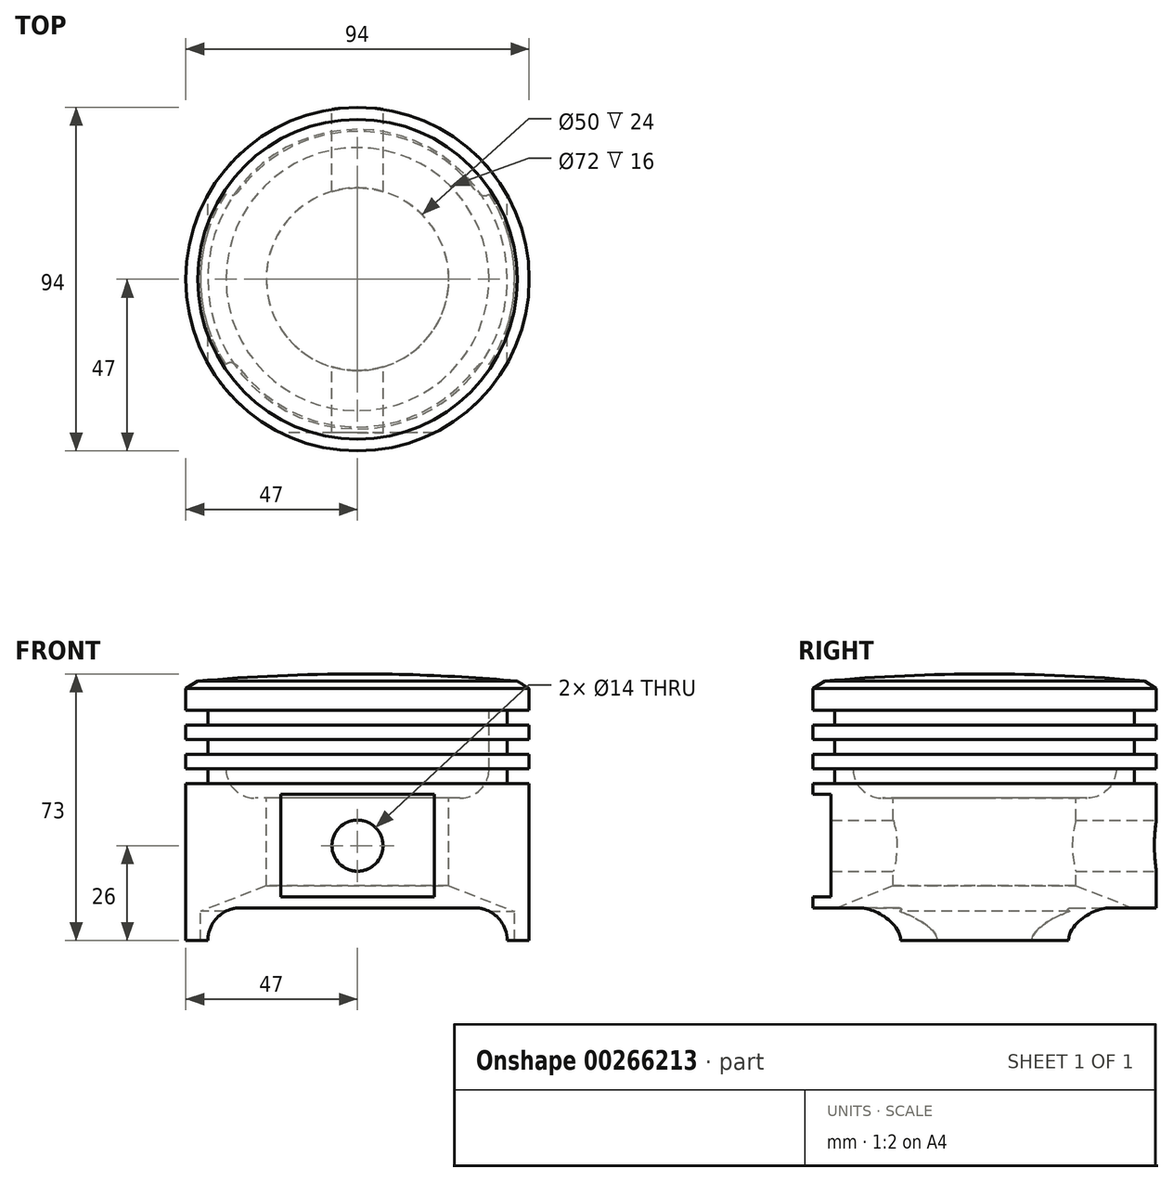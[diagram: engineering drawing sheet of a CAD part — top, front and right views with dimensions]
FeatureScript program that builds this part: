
annotation { "Feature Type Name" : "Feature", "Feature Type Description" : "" }
export const myFeature = defineFeature(function(context is Context, id is Id, definition is map)
    precondition{}
    {
        {
            var Q0;
            Q0=qCreatedBy(makeId("Front.planeOp"),FACE);
            var sketch = newSketch(context, id + "F0", { "sketchPlane" : qUnion([Q0])});
            skLineSegment(sketch, "E0", {"start": v(43.74, 89) * mm, "end": v(47, 87) * mm});
            skLineSegment(sketch, "E1", {"start": v(47, 87) * mm, "end": v(47, 81) * mm});
            skLineSegment(sketch, "E2", {"start": v(47, 81) * mm, "end": v(41, 81) * mm});
            skLineSegment(sketch, "E3", {"start": v(41, 81) * mm, "end": v(41, 77) * mm});
            skLineSegment(sketch, "E4", {"start": v(41, 77) * mm, "end": v(47, 77) * mm});
            skLineSegment(sketch, "E5", {"start": v(47, 77) * mm, "end": v(47, 73) * mm});
            skLineSegment(sketch, "E6", {"start": v(47, 73) * mm, "end": v(41, 73) * mm});
            skLineSegment(sketch, "E7", {"start": v(41, 73) * mm, "end": v(41, 69) * mm});
            skLineSegment(sketch, "E8", {"start": v(41, 69) * mm, "end": v(47, 69) * mm});
            skLineSegment(sketch, "E9", {"start": v(47, 69) * mm, "end": v(47, 65) * mm});
            skLineSegment(sketch, "E10", {"start": v(47, 65) * mm, "end": v(41, 65) * mm});
            skLineSegment(sketch, "E11", {"start": v(41, 65) * mm, "end": v(41, 61) * mm});
            skLineSegment(sketch, "E12", {"start": v(41, 61) * mm, "end": v(47, 61) * mm});
            skLineSegment(sketch, "E13", {"start": v(47, 61) * mm, "end": v(47, 57) * mm});
            skLineSegment(sketch, "E14", {"start": v(47, 57) * mm, "end": v(41, 57) * mm});
            skLineSegment(sketch, "E15", {"start": v(41, 57) * mm, "end": v(41, 33) * mm, "construction": true});
            skLineSegment(sketch, "E16", {"start": v(41, 33) * mm, "end": v(47, 33) * mm});
            skLineSegment(sketch, "E17", {"start": v(47, 33) * mm, "end": v(47, 18) * mm});
            skLineSegment(sketch, "E18.MirrorCS", {"start": v(-43.74, 89) * mm, "end": v(-47, 87) * mm, "construction": true});
            skLineSegment(sketch, "E19.MirrorCS", {"start": v(-47, 87) * mm, "end": v(-47, 81) * mm, "construction": true});
            skLineSegment(sketch, "E20.MirrorCS", {"start": v(-47, 81) * mm, "end": v(-41, 81) * mm, "construction": true});
            skLineSegment(sketch, "E21.MirrorCS", {"start": v(-41, 81) * mm, "end": v(-41, 77) * mm, "construction": true});
            skLineSegment(sketch, "E22.MirrorCS", {"start": v(-47, 61) * mm, "end": v(-47, 57) * mm, "construction": true});
            skLineSegment(sketch, "E23.MirrorCS", {"start": v(-41, 65) * mm, "end": v(-41, 61) * mm, "construction": true});
            skLineSegment(sketch, "E24.MirrorCS", {"start": v(-41, 73) * mm, "end": v(-41, 69) * mm, "construction": true});
            skLineSegment(sketch, "E25.MirrorCS", {"start": v(-47, 57) * mm, "end": v(-41, 57) * mm, "construction": true});
            skLineSegment(sketch, "E26.MirrorCS", {"start": v(-41, 57) * mm, "end": v(-41, 33) * mm, "construction": true});
            skLineSegment(sketch, "E27.MirrorCS", {"start": v(-47, 33) * mm, "end": v(-47, 18) * mm, "construction": true});
            skLineSegment(sketch, "E28.MirrorCS", {"start": v(-41, 33) * mm, "end": v(-47, 33) * mm, "construction": true});
            skLineSegment(sketch, "E29.MirrorCS", {"start": v(-41, 61) * mm, "end": v(-47, 61) * mm, "construction": true});
            skLineSegment(sketch, "E30.MirrorCS", {"start": v(-47, 65) * mm, "end": v(-41, 65) * mm, "construction": true});
            skLineSegment(sketch, "E31.MirrorCS", {"start": v(-47, 77) * mm, "end": v(-47, 73) * mm, "construction": true});
            skLineSegment(sketch, "E32.MirrorCS", {"start": v(-47, 73) * mm, "end": v(-41, 73) * mm, "construction": true});
            skLineSegment(sketch, "E33.MirrorCS", {"start": v(-47, 69) * mm, "end": v(-47, 65) * mm, "construction": true});
            skLineSegment(sketch, "E34.MirrorCS", {"start": v(-41, 77) * mm, "end": v(-47, 77) * mm, "construction": true});
            skLineSegment(sketch, "E35.MirrorCS", {"start": v(-41, 69) * mm, "end": v(-47, 69) * mm, "construction": true});
            skLineSegment(sketch, "E36", {"start": v(0, 0) * mm, "end": v(29, 0) * mm, "construction": true});
            skArc(sketch, "E37", {"start": v(47, 18) * mm, "mid": v(34.27, 12.73) * mm, "end": v(29, 0) * mm, "construction": true});
            skLineSegment(sketch, "E38", {"start": v(0, 91) * mm, "end": v(0, 0) * mm});
            skLineSegment(sketch, "E39", {"start": v(47, 57) * mm, "end": v(47, 33) * mm});
            skLineSegment(sketch, "E40", {"start": v(47, 18) * mm, "end": v(0, 18) * mm});
            skArc(sketch, "E41", {"start": v(43.74, 89) * mm, "mid": v(21.9, 90.5) * mm, "end": v(0, 91) * mm});
            skSolve(sketch);
        }
        {
            var Q0;
            Q0=makeQuery(id+"F0.imprint","IMPRINT",FACE,{"disambiguationData":[TD([[makeQuery(id+"F0.imprint","IMPRINT",EDGE,{"derivedFrom":sQuery(id+"F0.wireOp",EDGE,"E0")}),-1.0]])]});
            var Q1;
            Q1=sQuery(id+"F0.wireOp",EDGE,"E38");
            revolve(context, id + "F1", {"entities" : qUnion([Q0]), "axis" : qUnion([Q1]), "revolveType" : RevolveType.FULL});
        }
        {
            var Q0;
            Q0=qCreatedBy(makeId("Front.planeOp"),FACE);
            var sketch = newSketch(context, id + "F2", { "sketchPlane" : qUnion([Q0])});
            skCircle(sketch, "E42", {"center": v(0, 44) * mm, "radius": 7 * mm});
            skSolve(sketch);
        }
        {
            var Q0;
            Q0 = qSketchRegion(id + "F2", true);
            extrude(context, id + "F3", {"entities" : qUnion([Q0]), "operationType" : NewBodyOperationType.REMOVE, "endBound" : BoundingType.SYMMETRIC, "depth" : 144 * mm});
        }
        {
            var Q0;
            Q0=qCreatedBy(makeId("Front.planeOp"),FACE);
            var sketch = newSketch(context, id + "F4", { "sketchPlane" : qUnion([Q0])});
            skLineSegment(sketch, "E43.bottom", {"start": v(21, 58) * mm, "end": v(-21, 58) * mm});
            skLineSegment(sketch, "E43.top", {"start": v(21, 30) * mm, "end": v(-21, 30) * mm});
            skLineSegment(sketch, "E43.left", {"start": v(21, 58) * mm, "end": v(21, 30) * mm});
            skLineSegment(sketch, "E43.right", {"start": v(-21, 58) * mm, "end": v(-21, 30) * mm});
            skPoint(sketch, "E43.middle", {"position": v(0, 44) * mm});
            skCircle(sketch, "E44.0", {"center": v(0, 44) * mm, "radius": 7 * mm});
            skSolve(sketch);
        }
        {
            var Q0;
            Q0 = qSketchRegion(id + "F4", true);
            extrude(context, id + "F5", {"entities" : qUnion([Q0]), "operationType" : NewBodyOperationType.REMOVE, "depth" : 70.7 * mm, "hasSecondDirection" : true, "secondDirectionOppositeDirection" : false, "secondDirectionDepth" : 42 * mm});
        }
        {
            var Q0;
            Q0=qCreatedBy(makeId("Front.planeOp"),FACE);
            var sketch = newSketch(context, id + "F6", { "sketchPlane" : qUnion([Q0])});
            skLineSegment(sketch, "E45", {"start": v(0, -38.7) * mm, "end": v(0, 107.06) * mm});
            skLineSegment(sketch, "E46", {"start": v(0, 81) * mm, "end": v(36, 81) * mm});
            skLineSegment(sketch, "E47", {"start": v(36, 81) * mm, "end": v(36, 65) * mm});
            skLineSegment(sketch, "E48", {"start": v(28, 57) * mm, "end": v(25, 57) * mm});
            skLineSegment(sketch, "E49", {"start": v(25, 57) * mm, "end": v(25, 33) * mm});
            skLineSegment(sketch, "E50", {"start": v(25, 33) * mm, "end": v(43, 26) * mm});
            skLineSegment(sketch, "E51", {"start": v(43, 26) * mm, "end": v(43, 18) * mm});
            skLineSegment(sketch, "E52", {"start": v(43, 18) * mm, "end": v(0, 18) * mm});
            skLineSegment(sketch, "E53", {"start": v(41, 73) * mm, "end": v(41, 69) * mm});
            skPoint(sketch, "E54.visualSharp", {"position": v(36, 57) * mm});
            skArc(sketch, "E54.filletArc", {"start": v(28, 57) * mm, "mid": v(33.66, 59.34) * mm, "end": v(36, 65) * mm});
            skLineSegment(sketch, "E55.0", {"start": v(-47, 18) * mm, "end": v(47, 18) * mm});
            skSolve(sketch);
        }
        {
            var Q0;
            Q0 = qSketchRegion(id + "F6", true);
            var Q1;
            Q1=sQuery(id+"F6.wireOp",EDGE,"E45");
            revolve(context, id + "F7", {"operationType" : NewBodyOperationType.REMOVE, "entities" : qUnion([Q0]), "axis" : qUnion([Q1]), "revolveType" : RevolveType.FULL, "oppositeDirection" : true});
        }
        {
            var Q0;
            Q0=qCreatedBy(makeId("Front.planeOp"),FACE);
            var sketch = newSketch(context, id + "F8", { "sketchPlane" : qUnion([Q0])});
            skLineSegment(sketch, "E56", {"start": v(-32, 27) * mm, "end": v(32, 27) * mm});
            skLineSegment(sketch, "E57.0", {"start": v(-47, 18) * mm, "end": v(47, 18) * mm});
            skLineSegment(sketch, "E58", {"start": v(-41, 18) * mm, "end": v(-41, 18) * mm});
            skPoint(sketch, "E59.visualSharp", {"position": v(-41, 27) * mm});
            skArc(sketch, "E59.filletArc", {"start": v(-32, 27) * mm, "mid": v(-38.36, 24.36) * mm, "end": v(-41, 18) * mm});
            skArc(sketch, "E60.MirrorCS", {"start": v(32, 27) * mm, "mid": v(38.36, 24.36) * mm, "end": v(41, 18) * mm});
            skPoint(sketch, "E61.MirrorCS.end.orphan", {"position": v(41, 18) * mm});
            skPoint(sketch, "E62.orphan", {"position": v(41, 27) * mm});
            skSolve(sketch);
        }
        {
            var Q0;
            Q0 = qSketchRegion(id + "F8", true);
            extrude(context, id + "F9", {"entities" : qUnion([Q0]), "operationType" : NewBodyOperationType.REMOVE, "endBound" : BoundingType.SYMMETRIC, "depth" : 422.6 * mm});
        }
    });
